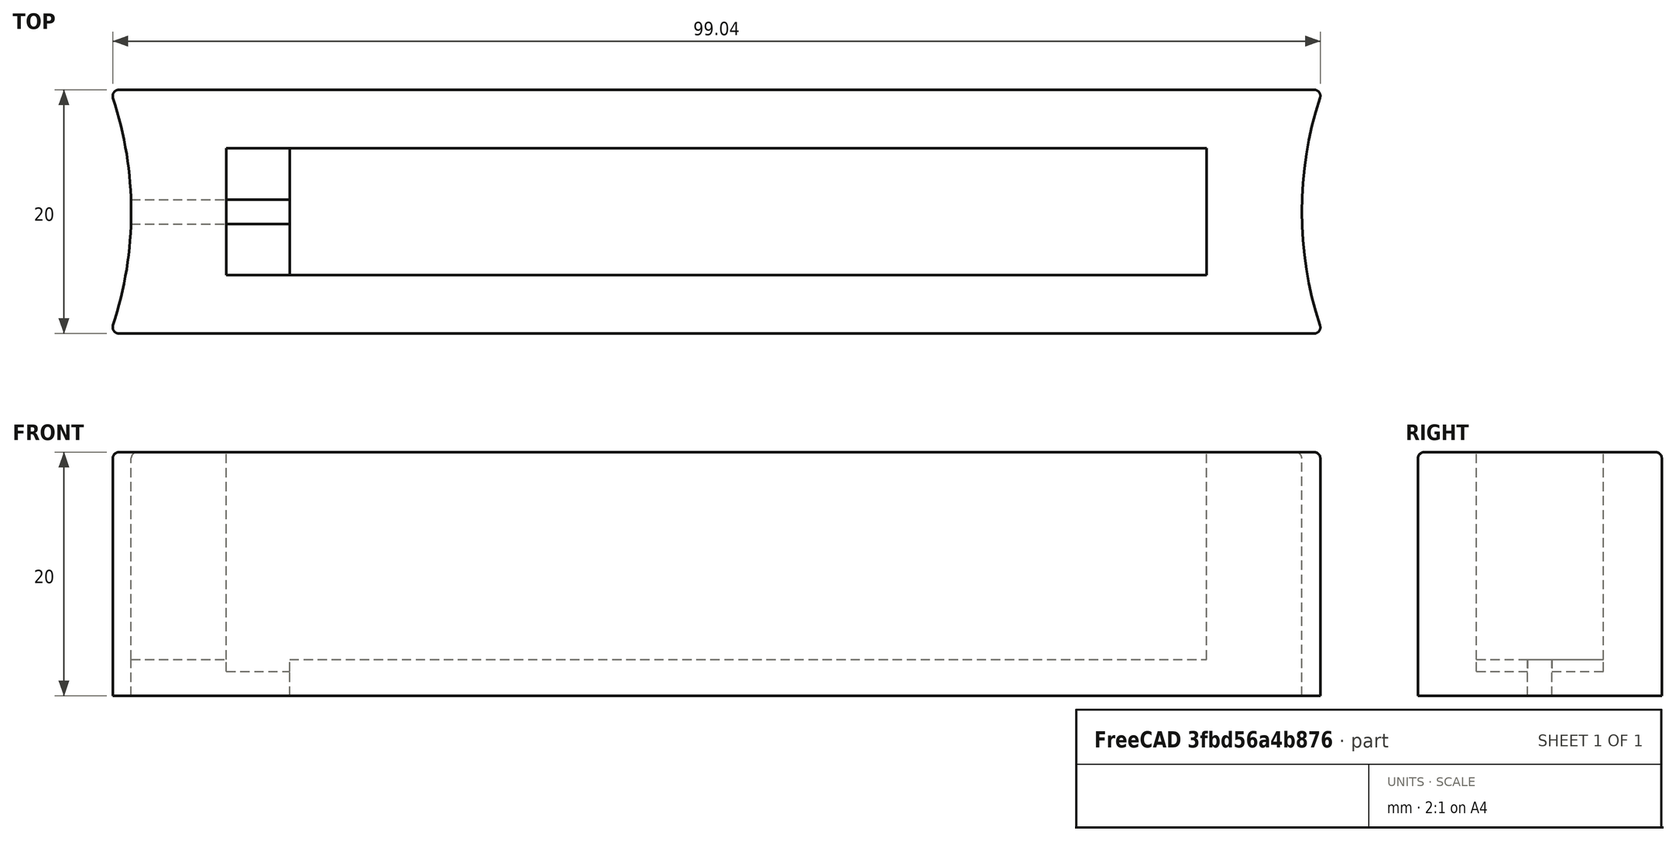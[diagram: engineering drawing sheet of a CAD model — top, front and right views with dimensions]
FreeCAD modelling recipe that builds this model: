
FCSTD DOCUMENT  (FreeCAD 0.18.4R)
Label: Socle_imp_3D_deco_led
License: All rights reserved
LicenseURL: http://en.wikipedia.org/wiki/All_rights_reserved
objects: Part::Cut×5, Part::Box×4, App::MeasureDistance×3, Part::Cylinder×2, Part::Fillet×2
note: 13 computed .brp shape members not serialized (recipe doc carries the construction recipe); baked Part::Feature solids carry a one-line shape summary decoded from their .brp

FEATURE [Part::Box] Box  label="Cube"
  AttacherType = Attacher::AttachEngine3D
  Height = 20
  Length = 100
  Width = 20
FEATURE [Part::Box] Box001  label="Cube001"
  AttacherType = Attacher::AttachEngine3D
  Height = 20
  Length = 80.4
  Placement = pos=(9.8,4.8,3) rot=(0,0,1;0rad)
  Width = 10.4
FEATURE [Part::Cut] Cut
  Base = -> Box
  Tool = -> Box001
FEATURE [Part::Box] Box002  label="Cube002"
  AttacherType = Attacher::AttachEngine3D
  Height = 3
  Length = 15
  Placement = pos=(0,9,0) rot=(0,0,1;0rad)
  Width = 2
FEATURE [Part::Cut] Cut001
  Base = -> Cut
  Tool = -> Box002
FEATURE [Part::Box] Box003  label="Cube003"
  AttacherType = Attacher::AttachEngine3D
  Height = 1
  Length = 5.2
  Placement = pos=(9.8,4.8,2) rot=(0,0,1;0rad)
  Width = 10.4
FEATURE [Part::Cut] Cut002
  Base = -> Cut001
  Tool = -> Box003
FEATURE [Part::Cylinder] Cylinder
  Angle = 360
  AttacherType = Attacher::AttachEngine3D
  Height = 20
  Placement = pos=(-28,10,0) rot=(0,0,1;0rad)
  Radius = 30
FEATURE [Part::Cylinder] Cylinder001
  Angle = 360
  AttacherType = Attacher::AttachEngine3D
  Height = 20
  Placement = pos=(128,10,0) rot=(0,0,1;0rad)
  Radius = 30
FEATURE [Part::Cut] Cut003
  Base = -> Cut002
  Tool = -> Cylinder001
FEATURE [Part::Cut] Cut004
  Base = -> Cut003
  Tool = -> Cylinder
FEATURE [Part::Fillet] Fillet
  Base = -> Cut004
  Edges = 4 edges r=0.5: [Edge11,Edge12,Edge13,Edge16]
FEATURE [Part::Fillet] Fillet001
  Base = -> Fillet
  Edges = 9 edges r=0.5: [Edge1,Edge2,Edge3,Edge4,Edge5,Edge6,Edge7,Edge8,Edge9]
FEATURE [App::MeasureDistance] Distance  label="Distance: 20,00 mm"
  Distance = 20
  P1 = (0.98838,0,0)
  P2 = (1.00257,0,20)
FEATURE [App::MeasureDistance] Distance001  label="Distance: 10,40 mm"
  Distance = 10.4
  P1 = (9.80607,4.8,20)
  P2 = (9.80156,15.2,20)
FEATURE [App::MeasureDistance] Distance002  label="Distance: 80,40 mm"
  Distance = 80.4
  P1 = (9.80004,4.79997,20)
  P2 = (90.2,4.80004,20)
